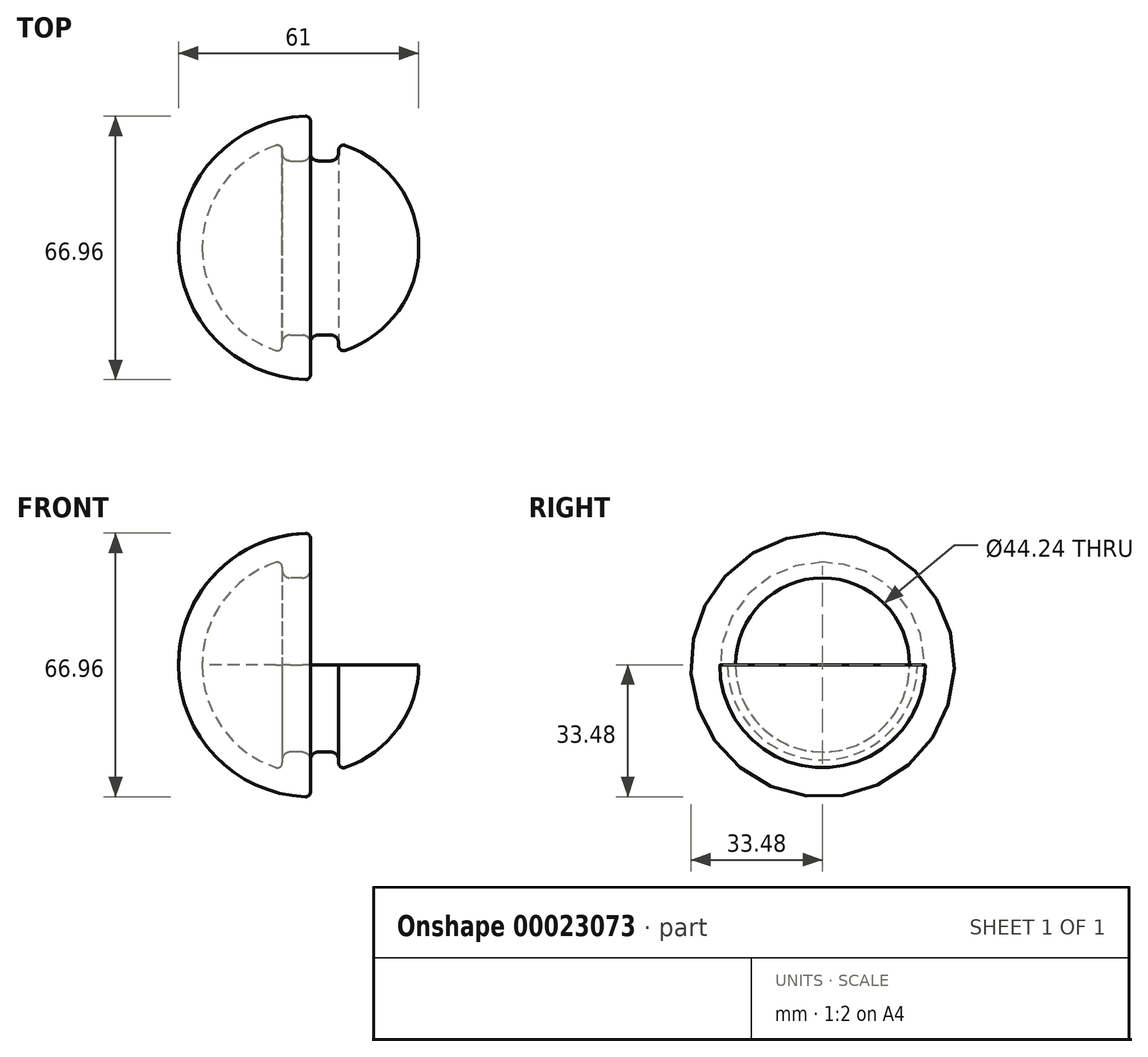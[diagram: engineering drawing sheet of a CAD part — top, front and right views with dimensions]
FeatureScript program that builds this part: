
annotation { "Feature Type Name" : "Feature", "Feature Type Description" : "" }
export const myFeature = defineFeature(function(context is Context, id is Id, definition is map)
    precondition{}
    {
        {
            var Q0;
            Q0=qCreatedBy(makeId("Front.planeOp"),FACE);
            var sketch = newSketch(context, id + "F0", { "sketchPlane" : qUnion([Q0])});
            skArc(sketch, "E0", {"start": v(-33.5, 0) * mm, "mid": v(-24.14, -23.22) * mm, "end": v(-1.3, -33.47) * mm});
            skLineSegment(sketch, "E1", {"start": v(0, -32.23) * mm, "end": v(0, -24.12) * mm});
            skArc(sketch, "E2", {"start": v(-27.5, 0) * mm, "mid": v(-22.35, -16.03) * mm, "end": v(-8.82, -26.05) * mm});
            skLineSegment(sketch, "E3", {"start": v(-7.16, -24.86) * mm, "end": v(-7.16, -24.12) * mm});
            skLineSegment(sketch, "E4", {"start": v(-5.16, -22.12) * mm, "end": v(-2, -22.12) * mm});
            skPoint(sketch, "E5.visualSharp", {"position": v(-7.16, -26.55) * mm});
            skArc(sketch, "E5.filletArc", {"start": v(-8.82, -26.05) * mm, "mid": v(-7.69, -25.88) * mm, "end": v(-7.16, -24.86) * mm});
            skPoint(sketch, "E6.visualSharp", {"position": v(-7.16, -22.12) * mm});
            skArc(sketch, "E6.filletArc", {"start": v(-5.16, -22.12) * mm, "mid": v(-6.58, -22.7) * mm, "end": v(-7.16, -24.12) * mm});
            skPoint(sketch, "E7.visualSharp", {"position": v(0, -22.12) * mm});
            skArc(sketch, "E7.filletArc", {"start": v(0, -24.12) * mm, "mid": v(-0.59, -22.7) * mm, "end": v(-2, -22.12) * mm});
            skPoint(sketch, "E8.visualSharp", {"position": v(0, -33.5) * mm});
            skArc(sketch, "E8.filletArc", {"start": v(-1.3, -33.47) * mm, "mid": v(-0.38, -33.13) * mm, "end": v(0, -32.23) * mm});
            skLineSegment(sketch, "E9", {"start": v(-33.5, 0) * mm, "end": v(-27.5, 0) * mm});
            skLineSegment(sketch, "E10", {"start": v(-27.5, 0) * mm, "end": v(0, 0) * mm});
            skLineSegment(sketch, "E11", {"start": v(0, 0) * mm, "end": v(0, -24.12) * mm});
            skLineSegment(sketch, "E12.MirrorCS", {"start": v(27.5, 0) * mm, "end": v(0, 0) * mm});
            skArc(sketch, "E13.MirrorCS", {"start": v(27.5, 0) * mm, "mid": v(22.35, -16.03) * mm, "end": v(8.82, -26.05) * mm});
            skArc(sketch, "E14.MirrorCS", {"start": v(8.82, -26.05) * mm, "mid": v(7.69, -25.88) * mm, "end": v(7.16, -24.86) * mm});
            skLineSegment(sketch, "E15.MirrorCS", {"start": v(7.16, -24.86) * mm, "end": v(7.16, -24.12) * mm});
            skArc(sketch, "E16.MirrorCS", {"start": v(5.16, -22.12) * mm, "mid": v(6.58, -22.7) * mm, "end": v(7.16, -24.12) * mm});
            skLineSegment(sketch, "E17.MirrorCS", {"start": v(5.16, -22.12) * mm, "end": v(2, -22.12) * mm});
            skArc(sketch, "E18.MirrorCS", {"start": v(0, -24.12) * mm, "mid": v(0.59, -22.7) * mm, "end": v(2, -22.12) * mm});
            skSolve(sketch);
        }
        {
            var Q0;
            Q0=makeQuery(id+"F0.imprint","IMPRINT",FACE,{"disambiguationData":[TD([[makeQuery(id+"F0.imprint","IMPRINT",EDGE,{"derivedFrom":sQuery(id+"F0.wireOp",EDGE,"E0")}),1.0]])]});
            var Q1;
            Q1=sQuery(id+"F0.wireOp",EDGE,"E9");
            revolve(context, id + "F1", {"entities" : qUnion([Q0]), "axis" : qUnion([Q1]), "revolveType" : RevolveType.FULL});
        }
        {
            var Q0;
            Q0=makeQuery(id+"F0.imprint","IMPRINT",FACE,{"disambiguationData":[TD([[makeQuery(id+"F0.imprint","IMPRINT",EDGE,{"derivedFrom":sQuery(id+"F0.wireOp",EDGE,"E2")}),1.0]])]});
            var Q1;
            Q1=makeQuery(id+"F0.imprint","IMPRINT",FACE,{"disambiguationData":[TD([[makeQuery(id+"F0.imprint","IMPRINT",EDGE,{"derivedFrom":sQuery(id+"F0.wireOp",EDGE,"E11")}),1.0]])]});
            var Q2;
            Q2=sQuery(id+"F0.wireOp",EDGE,"E10");
            revolve(context, id + "F2", {"entities" : qUnion([Q0, Q1]), "axis" : qUnion([Q2]), "revolveType" : RevolveType.SYMMETRIC, "angle" : 180 * degree});
        }
    });
